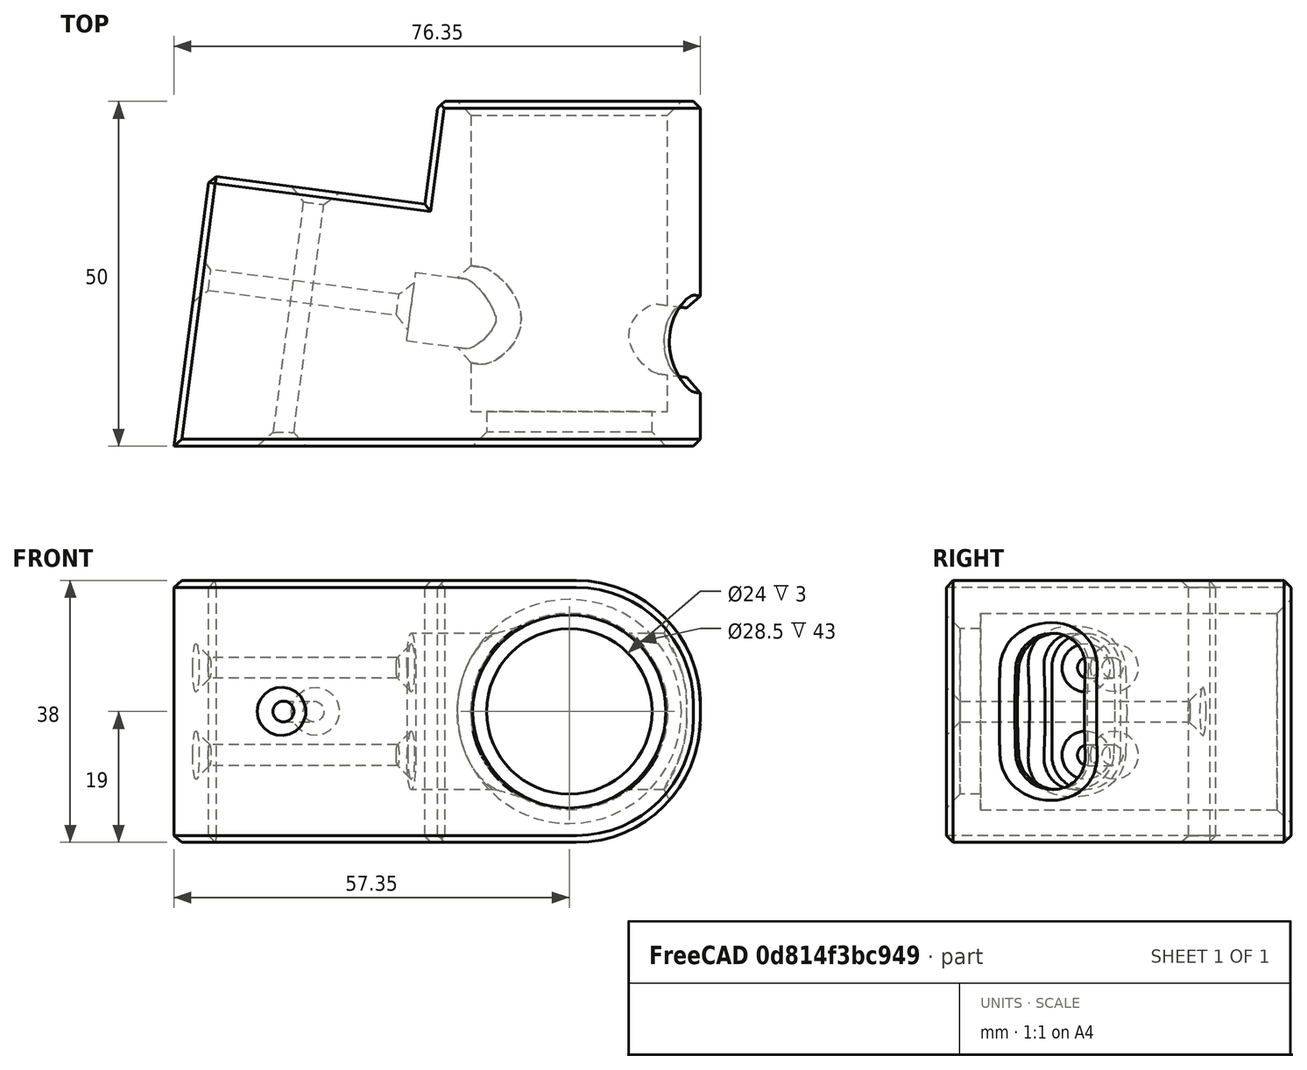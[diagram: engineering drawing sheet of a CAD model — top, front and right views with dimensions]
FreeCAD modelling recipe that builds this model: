
FCSTD DOCUMENT  (FreeCAD 0.18R16110 (Git))
Label: Support_mat_V3
License: All rights reserved
LicenseURL: http://en.wikipedia.org/wiki/All_rights_reserved
objects: PartDesign::Chamfer×13, Sketcher::SketchObject×10, PartDesign::Pocket×6, PartDesign::Pad×4, PartDesign::Fillet×1, PartDesign::Plane×1, PartDesign::Body×1, Mesh::Feature×1
note: 46 computed .brp shape members not serialized (recipe doc carries the construction recipe); baked Part::Feature solids carry a one-line shape summary decoded from their .brp

FEATURE [Sketcher::SketchObject] Sketch
  MapMode = 5
  Support = -> [XY_Plane]
  sketch-geometry (7):
    g0: LineSegment StartX=19 StartY=0 StartZ=0 EndX=-19 EndY=0 EndZ=0
    g1: LineSegment StartX=-61.9779 StartY=-85.1185 StartZ=0 EndX=-19 EndY=-90.7766 EndZ=0
    g2: LineSegment StartX=-19 StartY=-90.7766 StartZ=0 EndX=19 EndY=-90.7766 EndZ=0
    g3: LineSegment StartX=19 StartY=-90.7766 StartZ=0 EndX=19 EndY=0 EndZ=0
    g4: LineSegment StartX=-19 StartY=0 StartZ=0 EndX=-20.9579 EndY=-14.8717 EndZ=0
    g5: LineSegment StartX=-20.9579 StartY=-14.8717 StartZ=0 EndX=-52.1884 EndY=-10.7601 EndZ=0
    g6: LineSegment StartX=-52.1884 StartY=-10.7601 StartZ=0 EndX=-61.9779 EndY=-85.1185 EndZ=0
  constraints (20):
    c: PointOnObject(g0,g-1)
    c: Coincident(g1,g2)
    c: Horizontal(g2)
    c: Coincident(g2,g3)
    c: Coincident(g3,g0)
    c: Vertical(g3)
    c: Coincident(g0,g4)
    c: Coincident(g4,g5)
    c: Coincident(g5,g6)
    c: Coincident(g6,g1)
    c: Angle(g4,g0) = 1.7017
    c: Perpendicular(g4,g5)
    c: Perpendicular(g5,g6)
    c: Perpendicular(g1,g6)
    c: Distance(g5) = 31.5
    c: Distance(g4) = 15
    c: DistanceX(g0,g0) = 38
    c: Distance(g6) = 75
    c: Equal(g2,g0)
    c: Symmetric(g0,g0,g-2)
FEATURE [PartDesign::Pad] Pad
  Length = 38
  Length2 = 100
  Profile = -> Sketch
  Type = 0
FEATURE [Sketcher::SketchObject] Sketch001
  MapMode = 5
  Placement = pos=(0,0,0) rot=(0,0.707107,0.707107;3.14159rad)
  Support = -> [Pad]
  sketch-geometry (1):
    g0: Circle CenterX=0 CenterY=19 CenterZ=0 NormalX=0 NormalY=0 NormalZ=1 AngleXU=0 Radius=14.25
  constraints (3):
    c: Radius(g0) = 14.25
    c: Distance(g-1,g0) = 19
    c: PointOnObject(g0,g-2)
FEATURE [PartDesign::Pocket] Pocket
  BaseFeature = -> Pad
  Length = 100
  Length2 = 100
  Profile = -> Sketch001
  Type = 0
FEATURE [PartDesign::Fillet] Fillet
  Base = -> Pocket [Edge7,Edge8]
  BaseFeature = -> Pocket
  Radius = 18
FEATURE [Sketcher::SketchObject] Sketch002
  ExternalGeometry = -> [Fillet]
  MapMode = 5
  Placement = pos=(-49.9068,6.57036,0) rot=(-0.527011,0.600941,0.600941;4.11164rad)
  Support = -> [Fillet]
  sketch-geometry (4):
    g0: Circle CenterX=32.48 CenterY=25.3333 CenterZ=0 NormalX=0 NormalY=0 NormalZ=1 AngleXU=0 Radius=1.5
    g1: Circle CenterX=32.48 CenterY=12.6667 CenterZ=0 NormalX=0 NormalY=0 NormalZ=1 AngleXU=0 Radius=1.5
    g2: Circle CenterX=77.48 CenterY=25.3333 CenterZ=0 NormalX=0 NormalY=0 NormalZ=1 AngleXU=0 Radius=1.5
    g3: Circle CenterX=77.48 CenterY=12.6667 CenterZ=0 NormalX=0 NormalY=0 NormalZ=1 AngleXU=0 Radius=1.5
  constraints (12):
    c: Radius(g3) = 1.5
    c: Equal(g3,g2)
    c: Equal(g3,g0)
    c: Equal(g3,g1)
    c: Distance(g0,g-3) = 15
    c: Distance(g1,g-3) = 15
    c: Distance(g2,g-5) = 15
    c: Distance(g3,g-5) = 15
    c: DistanceY(g-1,g1) = 12.6667
    c: Distance(g0,g-4) = 12.6667
    c: Distance(g2,g-4) = 12.6667
    c: DistanceY(g-1,g3) = 12.6667
FEATURE [PartDesign::Pocket] Pocket001
  BaseFeature = -> Fillet
  Length = 100
  Length2 = 100
  Profile = -> Sketch002
  Type = 0
FEATURE [PartDesign::Plane] DatumPlane
  Length = 81.0007
  MapMode = 5
  Placement = pos=(-18.6763,2.45878,0) rot=(-0.527011,0.600941,0.600941;4.11164rad)
  ResizeMode = 0
  Support = -> [Pocket001]
  Width = 59.5477
FEATURE [Sketcher::SketchObject] Sketch003
  ExternalGeometry = -> [Pocket001]
  MapMode = 5
  Placement = pos=(-18.6763,2.45878,0) rot=(-0.527011,0.600941,0.600941;4.11164rad)
  Support = -> [DatumPlane]
  sketch-geometry (8):
    g0: ArcOfCircle CenterX=32.48 CenterY=25.3333 CenterZ=0 NormalX=0 NormalY=0 NormalZ=1 AngleXU=0 Radius=5 StartAngle=1.1e-15 EndAngle=3.14159
    g1: ArcOfCircle CenterX=32.48 CenterY=12.6667 CenterZ=0 NormalX=0 NormalY=0 NormalZ=1 AngleXU=0 Radius=5 StartAngle=3.14159 EndAngle=6.28319
    g2: LineSegment StartX=27.48 StartY=25.3333 StartZ=0 EndX=27.48 EndY=12.6667 EndZ=0
    g3: LineSegment StartX=37.48 StartY=25.3333 StartZ=0 EndX=37.48 EndY=12.6667 EndZ=0
    g4: ArcOfCircle CenterX=77.48 CenterY=25.3333 CenterZ=0 NormalX=0 NormalY=0 NormalZ=1 AngleXU=0 Radius=5 StartAngle=0 EndAngle=3.14159
    g5: ArcOfCircle CenterX=77.48 CenterY=12.6667 CenterZ=0 NormalX=0 NormalY=0 NormalZ=1 AngleXU=0 Radius=5 StartAngle=3.14159 EndAngle=6.28319
    g6: LineSegment StartX=72.48 StartY=25.3333 StartZ=0 EndX=72.48 EndY=12.6667 EndZ=0
    g7: LineSegment StartX=82.48 StartY=25.3333 StartZ=0 EndX=82.48 EndY=12.6667 EndZ=0
  constraints (16):
    c: Tangent(g0,g3) = 1.5708
    c: Tangent(g0,g2) = -1.5708
    c: Tangent(g2,g1) = -1.5708
    c: Tangent(g3,g1) = 1.5708
    c: Vertical(g2)
    c: Coincident(g0,g-3)
    c: Coincident(g1,g-4)
    c: Radius(g1) = 5
    c: Tangent(g4,g7) = 1.5708
    c: Tangent(g4,g6) = -1.5708
    c: Tangent(g6,g5) = -1.5708
    c: Tangent(g7,g5) = 1.5708
    c: Vertical(g6)
    c: Coincident(g4,g-5)
    c: Coincident(g5,g-6)
    c: Radius(g5) = 5
FEATURE [PartDesign::Pocket] Pocket002
  BaseFeature = -> Pocket001
  Length = 70
  Length2 = 100
  Profile = -> Sketch003
  Type = 0
FEATURE [Sketcher::SketchObject] Sketch004
  ExternalGeometry = -> [Pocket002,DatumPlane]
  MapMode = 5
  Placement = pos=(-2.2816,-17.3305,0) rot=(0.046297,0.706349,0.706349;3.04907rad)
  Support = -> [Pocket002]
  sketch-geometry (1):
    g0: Circle CenterX=34.8375 CenterY=19 CenterZ=0 NormalX=0 NormalY=0 NormalZ=1 AngleXU=0 Radius=1.5
  constraints (3):
    c: Radius(g0) = 1.5
    c: Distance(g0,g-3) = 19
    c: Distance(g0,g-4) = 15.5
FEATURE [PartDesign::Pocket] Pocket003
  BaseFeature = -> Pocket002
  Length = 50
  Length2 = 100
  Profile = -> Sketch004
  Type = 0
FEATURE [PartDesign::Chamfer] Chamfer
  Base = -> Pocket003 [Edge80,Edge82,Edge83,Edge85,Edge84]
  BaseFeature = -> Pocket003
  Size = 2
FEATURE [PartDesign::Chamfer] Chamfer001
  Base = -> Chamfer [Edge52,Edge48]
  BaseFeature = -> Chamfer
  Size = 2
FEATURE [PartDesign::Chamfer] Chamfer002
  Base = -> Chamfer001 [Edge70]
  BaseFeature = -> Chamfer001
  Size = 2
FEATURE [PartDesign::Chamfer] Chamfer003
  Base = -> Chamfer002 [Edge11]
  BaseFeature = -> Chamfer002
  Size = 2
FEATURE [PartDesign::Chamfer] Chamfer004
  Base = -> Chamfer003 [Edge11]
  BaseFeature = -> Chamfer003
  Size = 2
FEATURE [PartDesign::Chamfer] Chamfer005
  Base = -> Chamfer004 [Edge84]
  BaseFeature = -> Chamfer004
  Size = 1
FEATURE [Sketcher::SketchObject] Sketch006
  MapMode = 5
  Placement = pos=(0,0,38) rot=(0,0,1;0rad)
  sketch-geometry (3):
    g0: LineSegment StartX=1 StartY=-90.7766 StartZ=0 EndX=-61.6371 EndY=-82.5303 EndZ=0
    g1: LineSegment StartX=-61.6371 StartY=-82.5303 StartZ=0 EndX=-62.7228 EndY=-90.7766 EndZ=0
    g2: LineSegment StartX=-62.7228 StartY=-90.7766 StartZ=0 EndX=1 EndY=-90.7766 EndZ=0
  constraints (5):
    c: Coincident(g0,g1)
    c: Coincident(g1,g2)
    c: Coincident(g2,g0)
    c: Horizontal(g2)
    c: Perpendicular(g1,g0)
FEATURE [PartDesign::Pad] Pad002
  BaseFeature = -> Chamfer005
  Length = 38
  Length2 = 100
  Profile = -> Sketch006
  Reversed = true
  Type = 0
FEATURE [Sketcher::SketchObject] Sketch007
  MapMode = 5
  Placement = pos=(0,-90.7766,0) rot=(1,0,0;1.5708rad)
  Support = -> [Pad002]
  sketch-geometry (1):
    g0: Circle CenterX=0 CenterY=19 CenterZ=0 NormalX=0 NormalY=0 NormalZ=1 AngleXU=0 Radius=17
  constraints (3):
    c: PointOnObject(g0,g-2)
    c: Radius(g0) = 17
    c: DistanceY(g-1,g0) = 19
FEATURE [PartDesign::Pad] Pad003
  BaseFeature = -> Pad002
  Length = 5
  Length2 = 100
  Profile = -> Sketch007
  Reversed = true
  Type = 0
FEATURE [Sketcher::SketchObject] Sketch008
  ExternalGeometry = -> [Pad003]
  MapMode = 5
  Placement = pos=(0,-90.7766,0) rot=(1,0,0;1.5708rad)
  Support = -> [Pad003]
  sketch-geometry (1):
    g0: Circle CenterX=0 CenterY=19 CenterZ=0 NormalX=0 NormalY=0 NormalZ=1 AngleXU=0 Radius=12
  constraints (2):
    c: Coincident(g0,g-3)
    c: Radius(g0) = 12
FEATURE [PartDesign::Pocket] Pocket004
  BaseFeature = -> Pad003
  Length = 5
  Length2 = 100
  Profile = -> Sketch008
  Type = 0
FEATURE [PartDesign::Chamfer] Chamfer006
  Base = -> Pocket004 [Edge201]
  BaseFeature = -> Pocket004
  Size = 2
FEATURE [PartDesign::Chamfer] Chamfer007
  Base = -> Chamfer006 [Edge98,Edge194,Edge196,Edge193,Edge207,Edge197,Edge195,Edge175,Edge176]
  BaseFeature = -> Chamfer006
  Size = 1
FEATURE [PartDesign::Chamfer] Chamfer008
  Base = -> Chamfer007 [Edge167]
  BaseFeature = -> Chamfer007
  Size = 1
FEATURE [PartDesign::Chamfer] Chamfer009
  Base = -> Chamfer008 [Edge253,Edge251,Edge257,Edge255]
  BaseFeature = -> Chamfer008
  Size = 2
FEATURE [Sketcher::SketchObject] Sketch009
  MapMode = 5
  Placement = pos=(0,0,0) rot=(1,0,0;3.14159rad)
  Support = -> [Chamfer009]
  sketch-geometry (4):
    g0: LineSegment StartX=-70 StartY=110 StartZ=0 EndX=70 EndY=110 EndZ=0
    g1: LineSegment StartX=70 StartY=110 StartZ=0 EndX=70 EndY=50 EndZ=0
    g2: LineSegment StartX=70 StartY=50 StartZ=0 EndX=-70 EndY=50 EndZ=0
    g3: LineSegment StartX=-70 StartY=50 StartZ=0 EndX=-70 EndY=110 EndZ=0
  constraints (11):
    c: Coincident(g0,g1)
    c: Coincident(g1,g2)
    c: Coincident(g2,g3)
    c: Coincident(g3,g0)
    c: Horizontal(g0)
    c: Vertical(g1)
    c: Vertical(g3)
    c: Symmetric(g1,g2,g-2)
    c: DistanceY(g-1,g2) = 50
    c: DistanceX(g0,g0) = 140
    c: DistanceY(g3,g3) = 60
FEATURE [PartDesign::Pocket] Pocket005
  BaseFeature = -> Chamfer009
  Length = 50
  Length2 = 100
  Profile = -> Sketch009
  Type = 0
FEATURE [Sketcher::SketchObject] Sketch010
  ExternalGeometry = -> [Pocket005]
  MapMode = 5
  Placement = pos=(0,-50,0) rot=(1,0,0;1.5708rad)
  Support = -> [Pocket005]
  sketch-geometry (2):
    g0: Circle CenterX=0 CenterY=19 CenterZ=0 NormalX=0 NormalY=0 NormalZ=1 AngleXU=0 Radius=17
    g1: Circle CenterX=0 CenterY=19 CenterZ=0 NormalX=0 NormalY=0 NormalZ=1 AngleXU=0 Radius=12
  constraints (4):
    c: Coincident(g1,g-3)
    c: Coincident(g0,g1)
    c: Radius(g0) = 17
    c: Radius(g1) = 12
FEATURE [PartDesign::Pad] Pad004
  BaseFeature = -> Pocket005
  Length = 5
  Length2 = 100
  Profile = -> Sketch010
  Reversed = true
  Type = 0
FEATURE [PartDesign::Chamfer] Chamfer010
  Base = -> Pad004 [Edge136]
  BaseFeature = -> Pad004
  Size = 2
FEATURE [PartDesign::Chamfer] Chamfer011
  Base = -> Chamfer010 [Edge16]
  BaseFeature = -> Chamfer010
  Size = 2
FEATURE [PartDesign::Chamfer] Chamfer012
  Base = -> Chamfer011 [Edge2]
  BaseFeature = -> Chamfer011
  Size = 1
FEATURE [PartDesign::Body] Body
  Group = -> [Sketch,Pad,Sketch001,Pocket,Fillet,Sketch002,Pocket001,DatumPlane,Sketch003,Pocket002,Sketch004,Pocket003,Chamfer,Chamfer001,Chamfer002,Chamfer003,Chamfer004,Chamfer005,Sketch006,Pad002,Sketch007,Pad003,Sketch008,Pocket004,Chamfer006,Chamfer007,Chamfer008,Chamfer009,Sketch009,Pocket005,Sketch010,Pad004,Chamfer010,Chamfer011,Chamfer012]
  Origin = -> Origin
  Tip = -> Chamfer012
FEATURE [Mesh::Feature] Mesh  label="Body (Meshed)"
